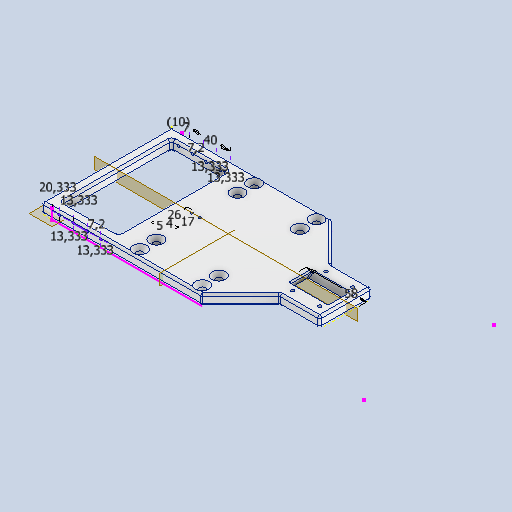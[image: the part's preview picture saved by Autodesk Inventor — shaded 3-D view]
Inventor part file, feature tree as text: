
AUTODESK INVENTOR PART (.ipt)
format: ipt  version: 2025 (Build 290162010, 162A)  size: 645,120 bytes
history: native  units: mm
features: sketch x14, hole x8, other x8, fillet x7, reference x6, extrude x5, projected_geometry x5, plane x4, chamfer x2, mirror x1, loft x1
ambient origin geometry x8: Origin, YZ Plane, XZ Plane, XY Plane, X Axis, Y Axis, Z Axis, Center Point
bodies: Volumenkörper1 (feature_tree)
feature tree (61):
  extrude  "main"  Depth=125.0mm
  hole  "BohrungLin"  [1 undecoded]
  plane  "Arbeitsebene4"
  extrude  "Extrusion7"  Depth=2.0mm
  fillet  "Rundung1"  Radius=77.0mm
  chamfer  "Fasen1"  Distance=3.5mm
  extrude  "Extrusion8"  Depth=2.0mm
  plane  "Arbeitsebene1"
  mirror  "Spiegeln1"
  plane  "Arbeitsebene2"
  hole  "Bohrung7"  [1 undecoded]
  loft  "Erhebung1"
  hole  "Bohrung10"  [1 undecoded]
  chamfer  "Fasen2"  Distance=2.0mm
  hole  "Bohrung11"  [1 undecoded]
  hole  "Bohrung12"  [1 undecoded]
  fillet  "Rundung5"  [1 undecoded]
  fillet  "Rundung6"  Radius=74.0mm
  fillet  "Rundung7"  Radius=16.0mm
  fillet  "Rundung8"  Radius=16.0mm
  fillet  "Rundung9"  Radius=70.0mm
  plane  "Arbeitsebene5"
  extrude  "Extrusion11"  Depth=2.0mm
  hole  "SeildurchgangL"  [1 undecoded]
  hole  "SeildurchgangR"  [1 undecoded]
  fillet  "Rundung10"  Radius=16.0mm
  sketch  "Skizze29"  dims[d128=20.0mm d129=3.5mm d130=0.0mm d131=2.5mm d132=1.0mm d133=2.0mm d134=45.0deg d135=2.0mm d136=1.0mm d137=2.0mm d138=5.0mm d139=0.0mm d154=1.567mm d155=5.0mm d156=4.0mm d157=2.0mm d158=90.0deg d159=6.3mm d160=20.594885mm d208=0.0mm d209=90.0deg d210=0.0mm d211=90.0deg d220=74.0mm d221=16.0mm d222=16.0mm d223=70.0mm d224=50.0mm d225=16.0mm d226=16.0mm d227=16.0mm d228=16.0mm d229=41.95mm d230=6.779mm d231=8.0mm d232=2.459mm d233=6.0mm d234=13.0mm d235=2.0mm d236=90.0deg d237=11.8mm d238=20.594885mm d242=37.5mm d243=2.0mm d244=45.0deg d245=40.0mm d246=32.0mm d247=26.0mm d248=2.0mm d249=3.242mm d250=8.0mm d251=4.0mm d252=2.0mm d253=90.0deg d254=8.0mm d255=20.594885mm d257=22.0mm d259=14.0mm d261=2.0mm d264=30.0mm d265=20.0mm d266=1.567mm d267=5.0mm d268=6.3mm d269=2.0mm d270=90.0deg d271=6.3mm d272=20.594885mm d273=2.0mm d274=22.0mm d275=20.207259mm d276=14.871377mm d277=3.0mm d278=25.980762mm d279=17.550869mm d280=1.0mm d281=1.0mm d282=1.0mm d283=1.0mm d284=10.0mm d285=10.0mm d286=10.3335mm d287=53.332mm d288=10.334mm d289=10.334mm d290=0.0mm d291=0.0mm d292=13.333mm d293=13.333mm d294=13.333mm d295=13.333333mm d296=2.0mm d297=42.0mm d298=14.0mm d299=62.5mm d300=26.0mm d301=5.0mm d302=58.0mm d303=5.0mm d304=0.0mm d305=17.0mm d306=4.0mm d307=1.567mm d308=4.0mm d309=10.4mm d310=2.0mm d311=90.0deg d312=9.0mm d313=20.594885mm]
  extrude  "Extrusion12"  Depth=2.0mm
  hole  "Bohrung13"  [1 undecoded]
  sketch  "Skizze1"  dims[d0=220.0mm d1=125.0mm]
  sketch  "Skizze2"  dims[d3=10.0mm d4=0.0mm d30=60.0mm]
  sketch  "Skizze4"  dims[d31=6.0mm d32=6.0mm d33=13.0mm d34=2.0mm d35=90.0deg d36=8.0mm d37=20.594885mm]
  sketch  "Skizze8"  dims[d50=2.459mm d51=1.0mm d52=4.0mm d53=2.0mm d54=90.0deg d55=1.0mm d56=20.594885mm]
  sketch  "Skizze12"  dims[d79=2.459mm d80=1.0mm d81=4.0mm d82=2.0mm d83=90.0deg d84=1.0mm d85=20.594885mm d88=7.5mm d89=77.0mm]
  projected_geometry  "Projizierte Kontur2"
  sketch  "Skizze13"  dims[d95=7.2mm]
  sketch  "Skizze15"  dims[d97=7.0mm]
  reference  "Referenz14"
  reference  "Referenz16"
  sketch  "Skizze22"  dims[d98=40.0mm]
  sketch  "Skizze23"  dims[d117=7.2mm]
  sketch  "Skizze25"  dims[d118=20.333333mm]
  sketch  "Skizze26"  dims[d120=13.333333mm]
  reference  "Referenz46"
  sketch  "Skizze27"  dims[d125=21.0mm]
  reference  "Referenz47"
  sketch  "Skizze28"  dims[d126=5.0mm]
  projected_geometry  "Projizierte Kontur3"
  projected_geometry  "Projizierte Kontur4"
  projected_geometry  "Projizierte Kontur5"
  projected_geometry  "Projizierte Kontur6"
  reference  "Referenz48"
  reference  "Referenz49"
  other  "<userpath>\GIT\HDVKBM\CAD\Krandemonstrator\Schlitten.iam"
  other  "Schlitten.iam"
  other  "DIN 7991 M6x16:2"
  other  "DIN 7991 M6x16:1"
  other  "Bedienhebel:1"
  other  "HebelhalterBlockBlind:1"
  other  "ISO 12633-2 - 20x20x2 - 200:1"
  other  "Sliderhalterpress:3"
note: 9 required parameter values undecoded (feature->parameter linkage not recoverable at this tier; creation-order binding heuristic only, values carry confidence <= 0.55)
